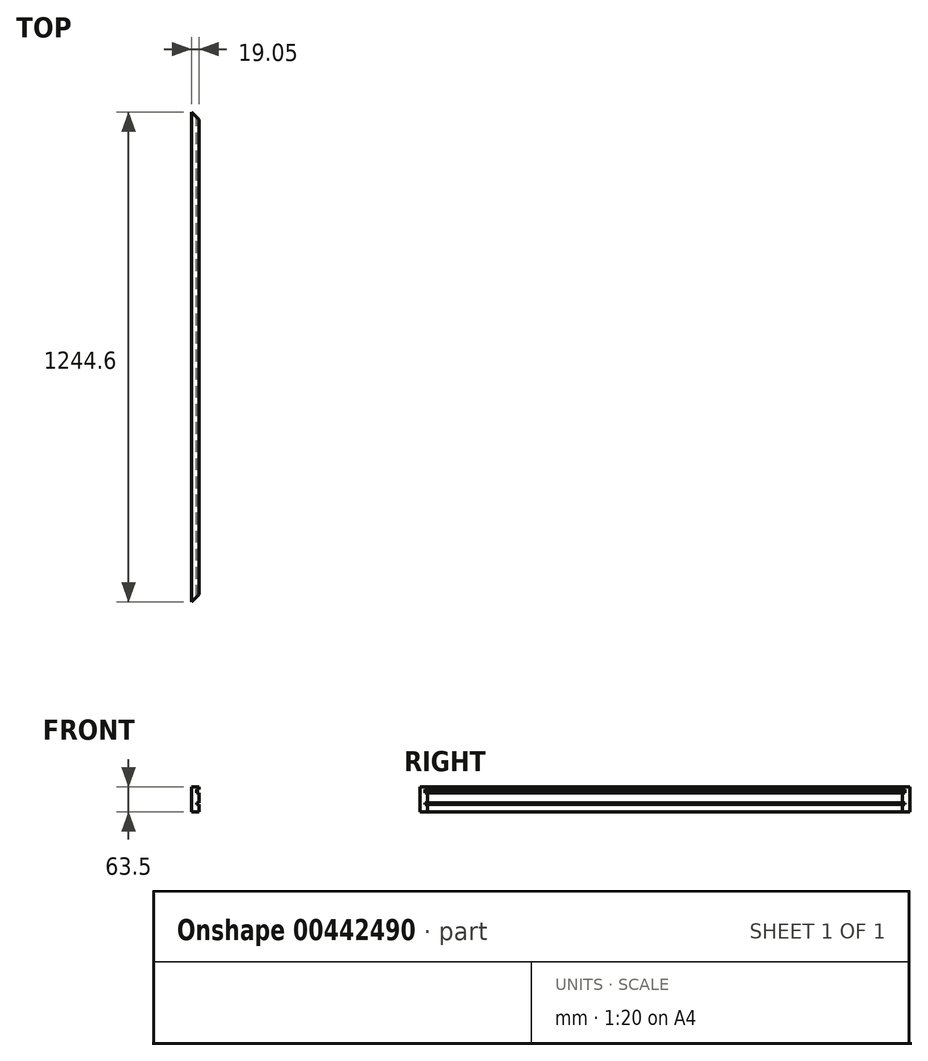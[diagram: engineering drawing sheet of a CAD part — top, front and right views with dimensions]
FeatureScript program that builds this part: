
annotation { "Feature Type Name" : "Feature", "Feature Type Description" : "" }
export const myFeature = defineFeature(function(context is Context, id is Id, definition is map)
    precondition{}
    {
        {
            var Q0;
            Q0=qCreatedBy(makeId("Front.planeOp"),FACE);
            var sketch = newSketch(context, id + "F0", { "sketchPlane" : qUnion([Q0])});
            skLineSegment(sketch, "E0", {"start": v(0, 63.5) * mm, "end": v(19.05, 63.5) * mm});
            skLineSegment(sketch, "E1", {"start": v(19.05, 63.5) * mm, "end": v(19.05, 57.15) * mm});
            skLineSegment(sketch, "E2", {"start": v(19.05, 57.15) * mm, "end": v(12.7, 57.15) * mm});
            skLineSegment(sketch, "E3", {"start": v(12.7, 57.15) * mm, "end": v(12.7, 48.51) * mm});
            skLineSegment(sketch, "E4", {"start": v(12.7, 48.51) * mm, "end": v(19.05, 48.51) * mm});
            skLineSegment(sketch, "E5", {"start": v(19.05, 48.51) * mm, "end": v(19.05, 23.11) * mm});
            skLineSegment(sketch, "E6", {"start": v(19.05, 23.11) * mm, "end": v(12.7, 23.11) * mm});
            skLineSegment(sketch, "E7", {"start": v(12.7, 23.11) * mm, "end": v(12.7, 19.05) * mm});
            skLineSegment(sketch, "E8", {"start": v(12.7, 19.05) * mm, "end": v(19.05, 19.05) * mm});
            skLineSegment(sketch, "E9", {"start": v(0, 0) * mm, "end": v(0, 63.5) * mm});
            skLineSegment(sketch, "E10", {"start": v(19.05, 19.05) * mm, "end": v(19.05, 0) * mm});
            skLineSegment(sketch, "E11", {"start": v(0, 0) * mm, "end": v(19.05, 0) * mm});
            skSolve(sketch);
        }
        {
            var Q0;
            Q0=makeQuery(id+"F0.imprint","IMPRINT",FACE,{"disambiguationData":[TD([[makeQuery(id+"F0.imprint","IMPRINT",EDGE,{"derivedFrom":sQuery(id+"F0.wireOp",EDGE,"E0")}),-1.0]])]});
            extrude(context, id + "F1", {"entities" : qUnion([Q0]), "depth" : 1244.6 * mm});
        }
        {
            var Q0;
            Q0=makeQuery(id+"F1.opExtrude","SWEPT_FACE",FACE,{"disambiguationData":[OSD([sQuery(id+"F0.wireOp",EDGE,"E0")])]});
            var sketch = newSketch(context, id + "F2", { "sketchPlane" : qUnion([Q0])});
            skLineSegment(sketch, "E12", {"start": v(0, 0) * mm, "end": v(0, -19.05) * mm});
            skLineSegment(sketch, "E13", {"start": v(0, -19.05) * mm, "end": v(19.05, -19.05) * mm});
            skLineSegment(sketch, "E14", {"start": v(19.05, -19.05) * mm, "end": v(0, 0) * mm});
            skLineSegment(sketch, "E15", {"start": v(0, -1244.6) * mm, "end": v(0, -1225.55) * mm});
            skLineSegment(sketch, "E16", {"start": v(0, -1225.55) * mm, "end": v(19.05, -1225.55) * mm});
            skLineSegment(sketch, "E17", {"start": v(19.05, -1225.55) * mm, "end": v(0, -1244.6) * mm});
            skSolve(sketch);
        }
        {
            var Q0;
            {var subQ0=sQuery(id+"F2.wireOp",EDGE,"E17");Q0=makeQuery(id+"F2.imprint","IMPRINT",FACE,{"disambiguationData":[TD([[makeQuery(id+"F2.imprint","IMPRINT",EDGE,{"derivedFrom":subQ0}),1.0]])]});}
            var Q1;
            {var subQ0=sQuery(id+"F2.wireOp",EDGE,"E14");Q1=makeQuery(id+"F2.imprint","IMPRINT",FACE,{"disambiguationData":[TD([[makeQuery(id+"F2.imprint","IMPRINT",EDGE,{"derivedFrom":subQ0}),-1.0]])]});}
            extrude(context, id + "F3", {"entities" : qUnion([Q0, Q1]), "operationType" : NewBodyOperationType.REMOVE, "oppositeDirection" : true, "depth" : 63.5 * mm});
        }
    });
